FCSTD DOCUMENT  (FreeCAD 1.1R42325 (Git))
Label: flat32
License: All rights reserved
objects: App::FeaturePython×50, Part::Part2DObjectPython×30, Sketcher::SketchObject×2, Image::ImagePlane×2, PartDesign::Body×1, Measure::MeasureDistanceDetached×1, App::Point×1
note: 35 computed .brp shape members not serialized (recipe doc carries the construction recipe); baked Part::Feature solids carry a one-line shape summary decoded from their .brp

FEATURE [Sketcher::SketchObject] Sketch
  ArcFitTolerance = 0
  AttachmentSupport = -> [XY_Plane]
  ExternalTypes = [0]
  FullyConstrained = false
  MakeInternals = false
  MapMode = 5
  sketch-geometry (129):
    g0: LineSegment StartX=-58.4533 StartY=41.9964 StartZ=0 EndX=59.4113 EndY=41.9964 EndZ=0
    g1: LineSegment StartX=72.1645 StartY=11.1126 StartZ=0 EndX=72.1645 EndY=-32.2771 EndZ=0
    g2: LineSegment StartX=-52.8636 StartY=37.943 StartZ=0 EndX=-12.1113 EndY=37.943 EndZ=0
    g3: LineSegment StartX=55.7454 StartY=36.2995 StartZ=0 EndX=55.7454 EndY=9.20361 EndZ=0
    g4: LineSegment StartX=-54.4028 StartY=-1.00339 StartZ=0 EndX=-54.4028 EndY=5.82203 EndZ=0
    g5: LineSegment StartX=-52.8636 StartY=37.943 StartZ=0 EndX=-52.8636 EndY=36.404 EndZ=0
    g6: LineSegment StartX=-52.8636 StartY=36.404 StartZ=0 EndX=-54.3721 EndY=36.404 EndZ=0
    g7: LineSegment StartX=21.2988 StartY=37.9406 StartZ=0 EndX=21.2988 EndY=20.6044 EndZ=0
    g8: LineSegment StartX=21.2988 StartY=20.6044 StartZ=0 EndX=11.216 EndY=20.6044 EndZ=0
    g9: LineSegment StartX=3.2959 StartY=21.0156 StartZ=0 EndX=3.2959 EndY=37.9443 EndZ=0
    g10: LineSegment StartX=20.18 StartY=36.5128 StartZ=0 EndX=20.18 EndY=21.0155 EndZ=0
    g11: LineSegment StartX=20.18 StartY=21.0155 StartZ=0 EndX=4.08358 EndY=21.0155 EndZ=0
    g12: LineSegment StartX=4.08358 StartY=21.0155 StartZ=0 EndX=4.08358 EndY=32.5222 EndZ=0
    g13: LineSegment StartX=11.116 StartY=37.9186 StartZ=0 EndX=11.116 EndY=32.5222 EndZ=0
    g14: LineSegment StartX=11.116 StartY=32.5222 StartZ=0 EndX=4.08358 EndY=32.5222 EndZ=0
    g15: LineSegment StartX=20.18 StartY=36.5128 StartZ=0 EndX=17.2316 EndY=36.5128 EndZ=0
    g16: LineSegment StartX=17.2316 StartY=36.5128 StartZ=0 EndX=17.2316 EndY=37.9186 EndZ=0
    g17: LineSegment StartX=11.116 StartY=37.9186 StartZ=0 EndX=17.2316 EndY=37.9186 EndZ=0
    g18: LineSegment StartX=21.2988 StartY=37.9406 StartZ=0 EndX=54.1032 EndY=37.9406 EndZ=0
    g19: LineSegment StartX=17.7483 StartY=21.0155 StartZ=0 EndX=17.7483 EndY=20.6044 EndZ=0
    g20: LineSegment StartX=11.216 StartY=20.6044 StartZ=0 EndX=11.216 EndY=21.0155 EndZ=0
    g21: LineSegment StartX=-10.9815 StartY=36.5115 StartZ=0 EndX=-10.9815 EndY=21.0156 EndZ=0
    g22: LineSegment StartX=-12.1113 StartY=8.35302 StartZ=0 EndX=-12.1113 EndY=37.943 EndZ=0
    g23: LineSegment StartX=-8.04197 StartY=37.9443 StartZ=0 EndX=-8.04197 EndY=36.5115 EndZ=0
    g24: LineSegment StartX=-8.04197 StartY=36.5115 StartZ=0 EndX=-10.9815 EndY=36.5115 EndZ=0
    g25: LineSegment StartX=-8.04197 StartY=37.9443 StartZ=0 EndX=3.2959 EndY=37.9443 EndZ=0
    g26: LineSegment StartX=-10.9815 StartY=21.0156 StartZ=0 EndX=3.2959 EndY=21.0156 EndZ=0
    g27: LineSegment StartX=11.216 StartY=20.6044 StartZ=0 EndX=-10.9715 EndY=20.6044 EndZ=0
    g28: LineSegment StartX=-10.9715 StartY=20.6044 StartZ=0 EndX=-10.9715 EndY=8.56171 EndZ=0
    g29: LineSegment StartX=-52.8709 StartY=8.97844 StartZ=0 EndX=-54.4014 EndY=8.97844 EndZ=0
    g30: LineSegment StartX=-54.4028 StartY=5.82203 StartZ=0 EndX=-52.8709 EndY=5.82203 EndZ=0
    g31: LineSegment StartX=-52.8709 StartY=5.82203 StartZ=0 EndX=-52.8709 EndY=6.21907 EndZ=0
    g32: LineSegment StartX=-52.8709 StartY=8.35302 StartZ=0 EndX=-12.1113 EndY=8.35302 EndZ=0
    g33: LineSegment StartX=-8.83892 StartY=6.21907 StartZ=0 EndX=-52.8709 EndY=6.21907 EndZ=0
    g34: LineSegment StartX=-10.9715 StartY=8.56171 StartZ=0 EndX=8.9857 EndY=8.56171 EndZ=0
    g35: LineSegment StartX=6.71846 StartY=3.07262 StartZ=0 EndX=-8.83892 EndY=3.07262 EndZ=0
    g36: LineSegment StartX=-8.83892 StartY=3.07262 StartZ=0 EndX=-8.83892 EndY=6.21907 EndZ=0
    g37: LineSegment StartX=-54.4014 StartY=8.97844 StartZ=0 EndX=-54.4028 EndY=36.404 EndZ=0
    g38: LineSegment StartX=-52.8709 StartY=8.35302 StartZ=0 EndX=-52.8709 EndY=8.97844 EndZ=0
    g39: LineSegment StartX=-72.0313 StartY=8.51763 StartZ=0 EndX=-58.4517 EndY=8.51763 EndZ=0
    g40: LineSegment StartX=-58.4517 StartY=6.82057 StartZ=0 EndX=-68.6696 EndY=6.82057 EndZ=0
    g41: LineSegment StartX=-68.6696 StartY=6.82057 StartZ=0 EndX=-68.6696 EndY=5.21862 EndZ=0
    g42: LineSegment StartX=-68.6696 StartY=5.21862 StartZ=0 EndX=-72.0313 EndY=5.21862 EndZ=0
    g43: LineSegment StartX=-72.0313 StartY=5.21862 StartZ=0 EndX=-72.0313 EndY=8.51763 EndZ=0
    g44: LineSegment StartX=-58.4517 StartY=-1.00339 StartZ=0 EndX=-54.4028 EndY=-1.00339 EndZ=0
    g45: LineSegment StartX=-58.4533 StartY=8.51763 StartZ=0 EndX=-58.4533 EndY=41.9964 EndZ=0
    g46: LineSegment StartX=-58.4517 StartY=6.82057 StartZ=0 EndX=-58.4517 EndY=-1.00339 EndZ=0
    g47: LineSegment StartX=8.97848 StartY=-28.496 StartZ=0 EndX=6.71846 EndY=-28.496 EndZ=0
    g48: LineSegment StartX=6.71846 StartY=-28.496 StartZ=0 EndX=6.71846 EndY=3.07262 EndZ=0
    g49: LineSegment StartX=8.9857 StartY=-22.0949 StartZ=0 EndX=9.78167 EndY=-22.0949 EndZ=0
    g50: LineSegment StartX=18.1214 StartY=-23.9331 StartZ=0 EndX=17.1396 EndY=-23.9331 EndZ=0
    g51: LineSegment StartX=8.97848 StartY=-28.496 StartZ=0 EndX=8.97848 EndY=-23.9331 EndZ=0
    g52: LineSegment StartX=8.9857 StartY=-22.0949 StartZ=0 EndX=8.9857 EndY=8.56171 EndZ=0
    g53: LineSegment StartX=17.1396 StartY=-22.0949 StartZ=0 EndX=17.1396 EndY=-23.9331 EndZ=0
    g54: LineSegment StartX=9.78167 StartY=-23.9331 StartZ=0 EndX=9.78167 EndY=-22.0949 EndZ=0
    g55: LineSegment StartX=9.78167 StartY=-23.9331 StartZ=0 EndX=8.97848 EndY=-23.9331 EndZ=0
    g56: LineSegment StartX=17.1396 StartY=-22.0949 StartZ=0 EndX=18.0438 EndY=-22.0949 EndZ=0
    g57: LineSegment StartX=18.0438 StartY=-21.4909 StartZ=0 EndX=21.002 EndY=-21.4909 EndZ=0
    g58: LineSegment StartX=18.0438 StartY=-22.0949 StartZ=0 EndX=18.0438 EndY=-21.4909 EndZ=0
    g59: LineSegment StartX=21.404 StartY=-23.9482 StartZ=0 EndX=21.404 EndY=-24.7569 EndZ=0
    g60: LineSegment StartX=21.404 StartY=-24.7569 StartZ=0 EndX=18.1214 EndY=-24.7569 EndZ=0
    g61: LineSegment StartX=18.1214 StartY=-24.7569 StartZ=0 EndX=18.1214 EndY=-23.9331 EndZ=0
    g62: LineSegment StartX=21.404 StartY=-23.9482 StartZ=0 EndX=25.4966 EndY=-23.9482 EndZ=0
    g63: LineSegment StartX=25.4966 StartY=-23.9482 StartZ=0 EndX=25.4966 EndY=-28.0142 EndZ=0
    g64: LineSegment StartX=27.1081 StartY=-28.0142 StartZ=0 EndX=25.4966 EndY=-28.0142 EndZ=0
    g65: LineSegment StartX=27.1081 StartY=-24.1438 StartZ=0 EndX=27.1081 EndY=-28.0142 EndZ=0
    g66: LineSegment StartX=42.9002 StartY=-24.1438 StartZ=0 EndX=27.1081 EndY=-24.1438 EndZ=0
    g67: LineSegment StartX=42.9002 StartY=-24.9375 StartZ=0 EndX=42.9002 EndY=-24.1438 EndZ=0
    g68: LineSegment StartX=46.1598 StartY=-24.9375 StartZ=0 EndX=42.9002 EndY=-24.9375 EndZ=0
    g69: LineSegment StartX=46.1598 StartY=-24.1343 StartZ=0 EndX=46.1598 EndY=-24.9375 EndZ=0
    g70: LineSegment StartX=67.0505 StartY=-24.1343 StartZ=0 EndX=46.1598 EndY=-24.1343 EndZ=0
    g71: LineSegment StartX=67.0505 StartY=-24.9529 StartZ=0 EndX=67.0505 EndY=-24.1343 EndZ=0
    g72: LineSegment StartX=68.5857 StartY=-24.9529 StartZ=0 EndX=67.0505 EndY=-24.9529 EndZ=0
    g73: LineSegment StartX=68.5857 StartY=-32.2771 StartZ=0 EndX=68.5857 EndY=-24.9529 EndZ=0
    g74: LineSegment StartX=68.5824 StartY=-18.1367 StartZ=0 EndX=72.1645 EndY=-18.1367 EndZ=0
    g75: LineSegment StartX=72.1645 StartY=-32.2771 StartZ=0 EndX=68.5857 EndY=-32.2771 EndZ=0
    g76: LineSegment StartX=68.5824 StartY=5.76906 StartZ=0 EndX=66.9498 EndY=5.76906 EndZ=0
    g77: LineSegment StartX=66.9285 StartY=-21.3814 StartZ=0 EndX=68.5824 EndY=-21.3814 EndZ=0
    g78: LineSegment StartX=68.5824 StartY=-21.3814 StartZ=0 EndX=68.5824 EndY=5.76906 EndZ=0
    g79: LineSegment StartX=66.9285 StartY=-22.3002 StartZ=0 EndX=45.9729 EndY=-22.3002 EndZ=0
    g80: LineSegment StartX=45.9729 StartY=-22.3002 StartZ=0 EndX=45.9729 EndY=-21.6864 EndZ=0
    g81: LineSegment StartX=66.9285 StartY=-21.3814 StartZ=0 EndX=66.9285 EndY=-22.3002 EndZ=0
    g82: LineSegment StartX=38.6082 StartY=-22.2862 StartZ=0 EndX=42.7166 EndY=-22.2862 EndZ=0
    g83: LineSegment StartX=42.7166 StartY=-22.2862 StartZ=0 EndX=42.7166 EndY=-21.6864 EndZ=0
    g84: LineSegment StartX=38.6082 StartY=-4.46395 StartZ=0 EndX=38.6082 EndY=-22.2862 EndZ=0
    g85: LineSegment StartX=45.9729 StartY=-21.6864 StartZ=0 EndX=42.7166 EndY=-21.6864 EndZ=0
    g86: LineSegment StartX=-58.4533 StartY=33.1051 StartZ=0 EndX=-54.4027 EndY=33.1051 EndZ=0
    g87: LineSegment StartX=-54.4018 StartY=16.0181 StartZ=0 EndX=-58.4533 EndY=16.0181 EndZ=0
    g88: LineSegment StartX=-22.6875 StartY=41.9964 StartZ=0 EndX=-22.6875 EndY=37.943 EndZ=0
    g89: LineSegment StartX=-39.8263 StartY=37.943 StartZ=0 EndX=-39.8263 EndY=41.9964 EndZ=0
    g90: LineSegment StartX=-0.273217 StartY=21.0156 StartZ=0 EndX=-0.273217 EndY=20.6044 EndZ=0
    g91: LineSegment StartX=-6.8366 StartY=20.6044 StartZ=0 EndX=-6.8366 EndY=21.0156 EndZ=0
    g92: LineSegment StartX=21.002 StartY=-4.46395 StartZ=0 EndX=38.6082 EndY=-4.46395 EndZ=0
    g93: LineSegment StartX=39.5091 StartY=-22.2862 StartZ=0 EndX=39.5091 EndY=-22.8134 EndZ=0
    g94: LineSegment StartX=21.002 StartY=-21.4909 StartZ=0 EndX=21.002 EndY=-4.46395 EndZ=0
    g95: LineSegment StartX=21.6887 StartY=-5.08078 StartZ=0 EndX=37.4984 EndY=-5.08078 EndZ=0
    g96: LineSegment StartX=37.4984 StartY=-5.08078 StartZ=0 EndX=37.4984 EndY=-19.1535 EndZ=0
    g97: LineSegment StartX=30.5655 StartY=-21.7835 StartZ=0 EndX=21.6887 EndY=-21.7835 EndZ=0
    g98: LineSegment StartX=21.6887 StartY=-21.7835 StartZ=0 EndX=21.6887 EndY=-5.08078 EndZ=0
    g99: LineSegment StartX=30.5655 StartY=-19.1535 StartZ=0 EndX=37.4984 EndY=-19.1535 EndZ=0
    g100: LineSegment StartX=30.5655 StartY=-21.7835 StartZ=0 EndX=30.5655 EndY=-19.1535 EndZ=0
    g101: LineSegment StartX=72.1645 StartY=-3.43392 StartZ=0 EndX=68.5824 EndY=-3.43392 EndZ=0
    g102: LineSegment StartX=58.5414 StartY=7.46309 StartZ=0 EndX=66.9498 EndY=7.46309 EndZ=0
    g103: LineSegment StartX=66.9498 StartY=7.46309 StartZ=0 EndX=66.9498 EndY=5.76906 EndZ=0
    g104: LineSegment StartX=58.5414 StartY=5.92032 StartZ=0 EndX=58.5414 EndY=7.46309 EndZ=0
    g105: LineSegment StartX=55.2287 StartY=5.92032 StartZ=0 EndX=58.5414 EndY=5.92032 EndZ=0
    g106: LineSegment StartX=55.2287 StartY=7.0292 StartZ=0 EndX=55.2287 EndY=5.92032 EndZ=0
    g107: LineSegment StartX=54.2209 StartY=9.20361 StartZ=0 EndX=55.7454 EndY=9.20361 EndZ=0
    g108: LineSegment StartX=54.2209 StartY=7.0292 StartZ=0 EndX=54.2209 EndY=9.20361 EndZ=0
    g109: LineSegment StartX=55.2287 StartY=7.0292 StartZ=0 EndX=54.2209 EndY=7.0292 EndZ=0
    g110: LineSegment StartX=55.7454 StartY=36.2995 StartZ=0 EndX=54.1032 EndY=36.2995 EndZ=0
    g111: LineSegment StartX=54.1032 StartY=36.2995 StartZ=0 EndX=54.1032 EndY=37.9406 EndZ=0
    g112: LineSegment StartX=55.7454 StartY=28.7724 StartZ=0 EndX=59.4076 EndY=28.7724 EndZ=0
    g113: LineSegment StartX=68.3386 StartY=11.1606 StartZ=0 EndX=55.7454 EndY=11.1606 EndZ=0
    g114: LineSegment StartX=65.906 StartY=38.0345 StartZ=0 EndX=59.4076 EndY=38.0345 EndZ=0
    g115: LineSegment StartX=59.4076 StartY=38.0345 StartZ=0 EndX=59.4076 EndY=11.1606 EndZ=0
    g116: LineSegment StartX=68.3386 StartY=11.1606 StartZ=0 EndX=68.3386 EndY=35.5504 EndZ=0
    g117: LineSegment StartX=65.906 StartY=35.5504 StartZ=0 EndX=68.3386 EndY=35.5504 EndZ=0
    g118: LineSegment StartX=65.906 StartY=38.0345 StartZ=0 EndX=65.906 EndY=35.5504 EndZ=0
    g119: LineSegment StartX=59.4113 StartY=39.6605 StartZ=0 EndX=70.0341 EndY=39.6605 EndZ=0
    g120: LineSegment StartX=59.4113 StartY=41.9964 StartZ=0 EndX=59.4113 EndY=39.6605 EndZ=0
    g121: LineSegment StartX=70.0341 StartY=11.1126 StartZ=0 EndX=72.3705 EndY=11.1126 EndZ=0
    g122: LineSegment StartX=70.0341 StartY=39.6605 StartZ=0 EndX=70.0341 EndY=11.1126 EndZ=0
    g123: LineSegment StartX=40.6854 StartY=41.9964 StartZ=0 EndX=40.6854 EndY=37.9406 EndZ=0
    g124: LineSegment StartX=23.5435 StartY=37.9406 StartZ=0 EndX=23.5435 EndY=41.9964 EndZ=0
    g125: LineSegment StartX=-12.1113 StartY=17.5417 StartZ=0 EndX=-10.9715 EndY=17.5417 EndZ=0
    g126: LineSegment StartX=-10.9715 StartY=10.2112 StartZ=0 EndX=-12.1113 EndY=10.2112 EndZ=0
    g127: LineSegment StartX=21.002 StartY=-19.139 StartZ=0 EndX=21.6887 EndY=-19.139 EndZ=0
    g128: LineSegment StartX=21.6887 StartY=-11.4103 StartZ=0 EndX=21.002 EndY=-11.4103 EndZ=0
  constraints (270):
    c: Coincident(g45,g0)
    c: Horizontal(g0)
    c: Vertical(g1)
    c: Horizontal(g2)
    c: Vertical(g3)
    c: Vertical(g4)
    c: Coincident(g5,g6)
    c: PointOnObject(g37,g6)
    c: Coincident(g5,g2)
    c: Perpendicular(g5,g6)
    c: Perpendicular(g6,g4)
    c: Coincident(g7,g8)
    c: Horizontal(g8)
    c: Vertical(g7)
    c: Vertical(g9)
    c: Coincident(g10,g11)
    c: Coincident(g11,g12)
    c: Horizontal(g11)
    c: Vertical(g10)
    c: Vertical(g12)
    c: Coincident(g13,g14)
    c: Horizontal(g14)
    c: Vertical(g13)
    c: Coincident(g15,g16)
    c: Horizontal(g15)
    c: Vertical(g16)
    c: Coincident(g17,g13)
    c: Coincident(g25,g9)
    c: Coincident(g14,g12)
    c: Coincident(g17,g16)
    c: Coincident(g15,g10)
    c: Coincident(g7,g18)
    c: Perpendicular(g18,g7)
    c: Vertical(g19)
    c: Vertical(g20)
    c: PointOnObject(g20,g11)
    c: PointOnObject(g19,g11)
    c: PointOnObject(g19,g8)
    c: Vertical(g21)
    c: Vertical(g22)
    c: Coincident(g23,g24)
    c: Horizontal(g24)
    c: Vertical(g23)
    c: Coincident(g2,g22)
    c: Coincident(g21,g24)
    c: Coincident(g23,g25)
    c: Horizontal(g26)
    c: Horizontal(g27)
    c: Coincident(g9,g26)
    c: Coincident(g21,g26)
    c: Coincident(g28,g27)
    c: Coincident(g8,g20)
    c: Coincident(g27,g8)
    c: Coincident(g30,g31)
    c: Coincident(g38,g29)
    c: Horizontal(g29)
    c: Horizontal(g30)
    c: Vertical(g31)
    c: Horizontal(g32)
    c: Horizontal(g33)
    c: Horizontal(g34)
    c: Coincident(g35,g36)
    c: Horizontal(g35)
    c: Vertical(g36)
    c: Coincident(g33,g36)
    c: Coincident(g30,g4)
    c: Coincident(g29,g37)
    c: Coincident(g31,g33)
    c: Coincident(g38,g32)
    c: Horizontal(g39)
    c: Horizontal(g40)
    c: Coincident(g41,g42)
    c: Coincident(g42,g43)
    c: Horizontal(g42)
    c: Vertical(g41)
    c: Vertical(g43)
    c: Horizontal(g44)
    c: Coincident(g41,g40)
    c: Coincident(g39,g43)
    c: PointOnObject(g45,g39)
    c: Coincident(g46,g40)
    c: Vertical(g46)
    c: Coincident(g4,g44)
    c: Coincident(g47,g48)
    c: Horizontal(g47)
    c: Vertical(g48)
    c: Coincident(g48,g35)
    c: Horizontal(g49)
    c: Horizontal(g50)
    c: Vertical(g51)
    c: Coincident(g51,g47)
    c: Coincident(g51,g55)
    c: Coincident(g52,g49)
    c: Coincident(g34,g52)
    c: Vertical(g52)
    c: Vertical(g53)
    c: Vertical(g54)
    c: Coincident(g50,g53)
    c: Coincident(g55,g54)
    c: Coincident(g49,g54)
    c: Coincident(g56,g53)
    c: Coincident(g58,g57)
    c: Horizontal(g57)
    c: Vertical(g58)
    c: Coincident(g59,g60)
    c: Coincident(g60,g61)
    c: Horizontal(g60)
    c: Vertical(g59)
    c: Vertical(g61)
    c: Coincident(g62,g63)
    c: Horizontal(g62)
    c: Vertical(g63)
    c: Coincident(g65,g64)
    c: Horizontal(g64)
    c: Vertical(g65)
    c: Coincident(g67,g66)
    c: Horizontal(g66)
    c: Vertical(g67)
    c: Coincident(g69,g68)
    c: Horizontal(g68)
    c: Vertical(g69)
    c: Coincident(g71,g70)
    c: Horizontal(g70)
    c: Vertical(g71)
    c: Coincident(g56,g58)
    c: Coincident(g61,g50)
    c: Coincident(g59,g62)
    c: Coincident(g66,g65)
    c: Coincident(g63,g64)
    c: Coincident(g68,g67)
    c: Coincident(g69,g70)
    c: Coincident(g73,g72)
    c: Horizontal(g72)
    c: Vertical(g73)
    c: Horizontal(g74)
    c: Horizontal(g75)
    c: Coincident(g77,g78)
    c: Coincident(g78,g76)
    c: Horizontal(g76)
    c: Horizontal(g77)
    c: Vertical(g78)
    c: Coincident(g79,g80)
    c: Coincident(g81,g79)
    c: Horizontal(g79)
    c: Vertical(g80)
    c: Vertical(g81)
    c: Coincident(g82,g83)
    c: Coincident(g84,g82)
    c: Horizontal(g82)
    c: Vertical(g83)
    c: Vertical(g84)
    c: Horizontal(g85)
    c: Coincident(g83,g85)
    c: Coincident(g85,g80)
    c: Coincident(g81,g77)
    c: PointOnObject(g74,g78)
    c: PointOnObject(g74,g1)
    c: Coincident(g73,g75)
    c: Coincident(g72,g71)
    c: Coincident(g75,g1)
    c: Horizontal(g86)
    c: Horizontal(g87)
    c: PointOnObject(g87,g45)
    c: PointOnObject(g87,g37)
    c: PointOnObject(g86,g45)
    c: PointOnObject(g86,g37)
    c: Vertical(g88)
    c: Vertical(g89)
    c: PointOnObject(g88,g0)
    c: PointOnObject(g88,g2)
    c: PointOnObject(g89,g2)
    c: PointOnObject(g89,g0)
    c: Vertical(g90)
    c: Vertical(g91)
    c: PointOnObject(g90,g26)
    c: PointOnObject(g90,g27)
    c: PointOnObject(g91,g26)
    c: PointOnObject(g91,g27)
    c: Coincident(g94,g92)
    c: Horizontal(g92)
    c: Vertical(g93)
    c: Vertical(g94)
    c: Coincident(g95,g96)
    c: Coincident(g97,g98)
    c: Coincident(g98,g95)
    c: Horizontal(g95)
    c: Horizontal(g97)
    c: Vertical(g96)
    c: Vertical(g98)
    c: Coincident(g100,g99)
    c: Horizontal(g99)
    c: Vertical(g100)
    c: Coincident(g97,g100)
    c: Coincident(g99,g96)
    c: Coincident(g94,g57)
    c: PointOnObject(g93,g82)
    c: Coincident(g84,g92)
    c: Horizontal(g101)
    c: PointOnObject(g101,g78)
    c: PointOnObject(g101,g1)
    c: Coincident(g102,g103)
    c: Coincident(g104,g102)
    c: Horizontal(g102)
    c: Vertical(g103)
    c: Vertical(g104)
    c: Coincident(g106,g105)
    c: Horizontal(g105)
    c: Vertical(g106)
    c: Coincident(g109,g108)
    c: Coincident(g108,g107)
    c: Horizontal(g107)
    c: Vertical(g108)
    c: Coincident(g107,g3)
    c: Coincident(g109,g106)
    c: Coincident(g104,g105)
    c: Coincident(g103,g76)
    c: Coincident(g110,g111)
    c: Horizontal(g110)
    c: Vertical(g111)
    c: Coincident(g18,g111)
    c: Coincident(g110,g3)
    c: Horizontal(g112)
    c: Horizontal(g113)
    c: Coincident(g114,g115)
    c: Horizontal(g114)
    c: Vertical(g115)
    c: Vertical(g116)
    c: Coincident(g118,g117)
    c: Horizontal(g117)
    c: Vertical(g118)
    c: Coincident(g117,g116)
    c: Coincident(g118,g114)
    c: PointOnObject(g112,g115)
    c: PointOnObject(g112,g3)
    c: PointOnObject(g113,g3)
    c: PointOnObject(g115,g113)
    c: Coincident(g113,g116)
    c: Coincident(g120,g119)
    c: Horizontal(g119)
    c: Vertical(g120)
    c: Coincident(g122,g121)
    c: Horizontal(g121)
    c: Vertical(g122)
    c: Coincident(g0,g120)
    c: Coincident(g119,g122)
    c: PointOnObject(g1,g121)
    c: Vertical(g123)
    c: Vertical(g124)
    c: PointOnObject(g123,g0)
    c: PointOnObject(g123,g18)
    c: PointOnObject(g124,g0)
    c: PointOnObject(g124,g18)
    c: Vertical(g28)
    c: Coincident(g22,g32)
    c: Coincident(g28,g34)
    c: Horizontal(g125)
    c: Horizontal(g126)
    c: PointOnObject(g126,g22)
    c: PointOnObject(g126,g28)
    c: PointOnObject(g125,g22)
    c: PointOnObject(g125,g28)
    c: Horizontal(g127)
    c: Horizontal(g128)
    c: PointOnObject(g128,g94)
    c: PointOnObject(g128,g98)
    c: PointOnObject(g127,g94)
    c: PointOnObject(g127,g98)
    c: DistanceY(g22,g22) = 29.59
    c: Distance(g22,g37) = 42.29
    c: Horizontal(g17)
FEATURE [PartDesign::Body] Body
  AllowCompound = false
  Group = -> [Sketch]
  Origin = -> Origin
FEATURE [Part::Part2DObjectPython] Clone2D  label="Sketch (2D)"  # Draft 2D object (typed FeaturePython)
  Fuse = false
  Objects = -> [Sketch]
  Scale = (122,122,122)
FEATURE [Image::ImagePlane] flat033
  XSize = 149.073
  YSize = 109.677
FEATURE [App::FeaturePython] Dimension  # Draft dimension (typed FeaturePython)
  Diameter = false
  Dimline = (-2854.54,1806.14,0)
  Direction = (0,0,0)
  Distance = 3622.43
  End = (-1477.69,1008.44,0)
  Normal = (0,0,1)
  Start = (-1477.69,4630.87,0)
FEATURE [App::FeaturePython] Dimension001  # Draft dimension (typed FeaturePython)
  Diameter = false
  Dimline = (6194.79,-201.526,0)
  Direction = (0,0,0)
  Distance = 2371.58
  End = (6625.96,853.939,0)
  Normal = (0,0,1)
  Start = (4712.65,-547.359,0)
FEATURE [Part::Part2DObjectPython] Rectangle  # Draft 2D object (typed FeaturePython)
  Area = 1.27559e+06
  ChamferSize = 0
  Columns = 1
  FilletRadius = 0
  Height = 1456.71
  Length = 875.663
  MakeFace = true
  Placement = pos=(7956.71,-832.865,0) rot=(0,0,1;1.5708rad)
  Rows = 1
FEATURE [Part::Part2DObjectPython] Rectangle001  # Draft 2D object (typed FeaturePython)
  Area = 1.27485e+06
  ChamferSize = 0
  Columns = 1
  FilletRadius = 0
  Height = 1923.18
  Length = 662.884
  MakeFace = true
  Placement = pos=(4784.29,-2496.31,0) rot=(0,0,1;0rad)
  Rows = 1
FEATURE [Part::Part2DObjectPython] Rectangle002  # Draft 2D object (typed FeaturePython)
  Area = 1.72525e+06
  ChamferSize = 0
  Columns = 1
  FilletRadius = 0
  Height = 654.7
  Length = 2635.17
  MakeFace = true
  Placement = pos=(5496.27,-2561.78,0) rot=(0,0,1;0rad)
  Rows = 1
FEATURE [Part::Part2DObjectPython] Rectangle006  # Draft 2D object (typed FeaturePython)
  Area = 833413
  ChamferSize = 0
  Columns = 1
  FilletRadius = 0
  Height = 455.621
  Length = 1829.18
  MakeFace = true
  Placement = pos=(2767.78,-510.925,0) rot=(0,0,1;0rad)
  Rows = 1
FEATURE [Part::Part2DObjectPython] Rectangle010  # Draft 2D object (typed FeaturePython)
  Area = 1.30156e+06
  ChamferSize = 0
  Columns = 1
  FilletRadius = 0
  Height = 2000.12
  Length = 650.74
  MakeFace = true
  Placement = pos=(-2129.21,2192.92,0) rot=(0,0,1;0rad)
  Rows = 1
FEATURE [Part::Part2DObjectPython] Rectangle011  # Draft 2D object (typed FeaturePython)
  Area = 2632188
  ChamferSize = 0
  Columns = 1
  FilletRadius = 0
  Height = 1880
  Length = 1400.1
  MakeFace = true
  Placement = pos=(-4543.16,1040.33,0) rot=(0,0,1;0rad)
  Rows = 1
FEATURE [Part::Part2DObjectPython] Rectangle012  # Draft 2D object (typed FeaturePython)
  Area = 732013
  ChamferSize = 0
  Columns = 1
  FilletRadius = 0
  Height = 609.737
  Length = 1200.54
  MakeFace = true
  Placement = pos=(-6502.33,1684,0) rot=(0,0,1;0rad)
  Rows = 1
FEATURE [Part::Part2DObjectPython] Rectangle013  # Draft 2D object (typed FeaturePython)
  Area = 850265
  ChamferSize = 0
  Columns = 1
  FilletRadius = 0
  Height = 459.801
  Length = 1849.2
  MakeFace = true
  Placement = pos=(-4771.15,4096.59,0) rot=(0,0,1;0rad)
  Rows = 1
FEATURE [App::FeaturePython] Dimension002  # Draft dimension (typed FeaturePython)
  Diameter = false
  Dimline = (4845.95,4276.18,0)
  Direction = (0,0,0)
  Distance = 2085.32
  End = (4959.33,4626.19,0)
  Normal = (0,0,1)
  Start = (2874.01,4626.19,0)
FEATURE [App::FeaturePython] Dimension003  # Draft dimension (typed FeaturePython)
  Diameter = false
  Dimline = (-3021.5,4294.46,0)
  Direction = (0,0,0)
  Distance = 2088.74
  End = (-2767.22,4627.45,0)
  Normal = (0,0,1)
  Start = (-4855.96,4627.45,0)
FEATURE [App::FeaturePython] Dimension004  # Draft dimension (typed FeaturePython)
  Diameter = false
  Dimline = (-6208.59,1996.06,0)
  Direction = (0,0,0)
  Distance = 2083.38
  End = (-6636.1,1953.91,0)
  Normal = (0,0,1)
  Start = (-6636.1,4037.28,0)
FEATURE [App::FeaturePython] Dimension005  # Draft dimension (typed FeaturePython)
  Diameter = false
  Dimline = (7840.76,-2175.53,0)
  Direction = (0,0,0)
  Distance = 1785.32
  End = (8367.62,-2208.65,0)
  Normal = (0,0,1)
  Start = (8367.62,-423.327,0)
FEATURE [App::FeaturePython] Dimension006  # Draft dimension (typed FeaturePython)
  Diameter = false
  Dimline = (6407.54,1358.86,0)
  Direction = (0,0,0)
  Distance = 2158.53
  End = (6801,1351.5,0)
  Normal = (0,0,1)
  Start = (6801,3510.03,0)
FEATURE [App::FeaturePython] Dimension007  # Draft dimension (typed FeaturePython)
  Diameter = false
  Dimline = (2086.67,4371.72,0)
  Direction = (0,0,0)
  Distance = 744.477
  End = (2099.36,4625.62,0)
  Normal = (0,0,1)
  Start = (1354.88,4625.62,0)
FEATURE [Part::Part2DObjectPython] Rectangle015  # Draft 2D object (typed FeaturePython)
  Area = 707177
  ChamferSize = 0
  Columns = 1
  FilletRadius = 0
  Height = 589.235
  Length = 1200.16
  MakeFace = true
  Placement = pos=(-6447.74,3373.47,0) rot=(0,0,1;0rad)
  Rows = 1
FEATURE [App::FeaturePython] Dimension008  # Draft dimension (typed FeaturePython)
  Diameter = false
  Dimline = (-2339.12,2134.76,0)
  Direction = (0,0,0)
  Distance = 2489.46
  End = (-1486.01,2134.76,0)
  Normal = (0,0,1)
  Start = (-1482.33,4624.22,0)
FEATURE [App::FeaturePython] Dimension009  # Draft dimension (typed FeaturePython)
  Diameter = false
  Dimline = (6598.51,3522.63,0)
  Direction = (0,0,0)
  Distance = 900
  End = (6800,3500,0)
  Normal = (0,0,1)
  Start = (6800,4400,0)
FEATURE [App::FeaturePython] Dimension010  # Draft dimension (typed FeaturePython)
  Diameter = false
  Dimline = (8282.17,3828.92,0)
  Direction = (0,0,0)
  Distance = 1092.13
  End = (8341.01,4200.32,0)
  Normal = (0,0,1)
  Start = (7248.88,4200.32,0)
FEATURE [App::FeaturePython] Dimension011  # Draft dimension (typed FeaturePython)
  Diameter = false
  Dimline = (8000,4200,0)
  Direction = (0,0,0)
  Distance = 794.276
  End = (8043.15,4395.21,0)
  Normal = (0,0,1)
  Start = (7248.88,4395.21,0)
FEATURE [App::FeaturePython] Dimension012  # Draft dimension (typed FeaturePython)
  Diameter = false
  Dimline = (7787.35,1363.16,0)
  Direction = (0,0,0)
  Distance = 3269.7
  End = (7248.39,1363.16,0)
  Normal = (0,0,1)
  Start = (7248.39,4632.86,0)
FEATURE [Part::Part2DObjectPython] Wire  # Draft 2D object (typed FeaturePython)
  Area = 0
  ChamferSize = 0
  Closed = false
  End = (-6400,3700,0)
  FilletRadius = 0
  Length = 6200
  MakeFace = true
  Placement = pos=(-1500,2400,0) rot=(0,0,1;0rad)
  Points = (4) [(0,0,0),(-900,0,0),(-900,1300,0),(-4900,1300,0)]
  Start = (-1500,2400,0)
  Subdivisions = 0
FEATURE [App::FeaturePython] Dimension013  # Draft dimension (typed FeaturePython)
  Diameter = false
  Dimline = (-5400,4500,0)
  Direction = (0,0,0)
  Distance = 600
  End = (-5700,4000,0)
  Normal = (0,0,1)
  Start = (-5700,4600,0)
FEATURE [App::FeaturePython] Dimension014  # Draft dimension (typed FeaturePython)
  Diameter = false
  Dimline = (8200,-1600,0)
  Direction = (0,0,0)
  Distance = 1700
  End = (8300,-2500,0)
  Normal = (0,0,1)
  Start = (8300,-800,0)
FEATURE [Sketcher::SketchObject] Sketch001
  ArcFitTolerance = 0
  ExternalTypes = [0]
  FullyConstrained = true
  MakeInternals = false
FEATURE [Measure::MeasureDistanceDetached] Distance  label="Distance: 6568.63 mm"
  Distance = 6568.63
  DistanceX = 6567.14
  DistanceY = 139.939
  DistanceZ = 0
  Position1 = (1093.73,-2248.34,0)
  Position2 = (7660.87,-2388.28,0)
FEATURE [Part::Part2DObjectPython] Line  # Draft 2D object (typed FeaturePython)
  Area = 0
  ChamferSize = 0
  Closed = false
  End = (-6249.14,4623.07,0)
  FilletRadius = 0
  Length = 529.719
  MakeFace = true
  Placement = pos=(-6639.07,4264.53,0) rot=(0,0,1;0rad)
  Points = (2) [(0,0,0),(389.936,358.542,0)]
  Start = (-6639.07,4264.53,0)
  Subdivisions = 0
FEATURE [Part::Part2DObjectPython] Line001  # Draft 2D object (typed FeaturePython)
  Area = 0
  ChamferSize = 0
  Closed = false
  End = (6797.11,4214.68,0)
  FilletRadius = 0
  Length = 578.325
  MakeFace = true
  Placement = pos=(6388.17,4623.62,0) rot=(0,0,1;0rad)
  Points = (2) [(0,0,0),(408.938,-408.938,0)]
  Start = (6388.17,4623.62,0)
  Subdivisions = 0
FEATURE [Part::Part2DObjectPython] Line002  # Draft 2D object (typed FeaturePython)
  Area = 0
  ChamferSize = 0
  Closed = false
  End = (4400,4600,0)
  FilletRadius = 0
  Length = 1200
  MakeFace = true
  Placement = pos=(3200,4600,0) rot=(0,0,1;0rad)
  Points = (2) [(0,0,0),(1200,0,0)]
  Start = (3200,4600,0)
  Subdivisions = 0
FEATURE [Part::Part2DObjectPython] Line003  # Draft 2D object (typed FeaturePython)
  Area = 0
  ChamferSize = 0
  Closed = false
  End = (5100,4600,0)
  FilletRadius = 0
  Length = 1200
  MakeFace = true
  Placement = pos=(6300,4600,0) rot=(0,0,1;0rad)
  Points = (2) [(0,0,0),(-1200,0,0)]
  Start = (6300,4600,0)
  Subdivisions = 0
FEATURE [Part::Part2DObjectPython] Line004  # Draft 2D object (typed FeaturePython)
  Area = 0
  ChamferSize = 0
  Closed = false
  End = (4500,4600,0)
  FilletRadius = 0
  Length = 500
  MakeFace = true
  Placement = pos=(5000,4600,0) rot=(0,0,1;0rad)
  Points = (2) [(0,0,0),(-500,0,0)]
  Start = (5000,4600,0)
  Subdivisions = 0
FEATURE [App::FeaturePython] Dimension015  # Draft dimension (typed FeaturePython)
  Diameter = false
  Dimline = (2300,-200,0)
  Direction = (0,0,0)
  Distance = 5200
  End = (3200,-600,0)
  Normal = (0,0,1)
  Start = (3200,4600,0)
FEATURE [App::FeaturePython] Dimension016  # Draft dimension (typed FeaturePython)
  Diameter = false
  Dimline = (6500,3100,0)
  Direction = (0,0,0)
  Distance = 4200
  End = (6800,4400,0)
  Normal = (0,0,1)
  Start = (2600,4400,0)
FEATURE [App::FeaturePython] Dimension017  # Draft dimension (typed FeaturePython)
  Diameter = false
  Dimline = (6400,4300,0)
  Direction = (0,0,0)
  Distance = 3200
  End = (6400,4500,0)
  Normal = (0,0,1)
  Start = (3200,4500,0)
FEATURE [App::FeaturePython] Dimension018  # Draft dimension (typed FeaturePython)
  Diameter = false
  Dimline = (6400,500,0)
  Direction = (0,0,0)
  Distance = 4152.84
  End = (6600,1000,0)
  Normal = (0,0,1)
  Start = (2447.29,966.029,0)
FEATURE [Part::Part2DObjectPython] Rectangle017  # Draft 2D object (typed FeaturePython)
  Area = 45600
  ChamferSize = 0
  Columns = 1
  FilletRadius = 0
  Height = 760
  Length = 60
  MakeFace = true
  Placement = pos=(2300,800,0) rot=(0,0,1;0rad)
  Rows = 1
FEATURE [App::FeaturePython] Dimension019  # Draft dimension (typed FeaturePython)
  Diameter = false
  Dimline = (2883.44,-2921.19,0)
  Direction = (0,0,0)
  Distance = 259.05
  End = (2797.73,-2921.19,0)
  Normal = (0,0,1)
  Start = (2797.73,-2662.14,0)
FEATURE [App::FeaturePython] Dimension020  # Draft dimension (typed FeaturePython)
  Diameter = false
  Dimline = (2650.24,-2757.17,0)
  Direction = (0,0,0)
  Distance = 87.6201
  End = (2650.24,-2500.02,0)
  Normal = (0,0,1)
  Start = (2562.62,-2500.02,0)
FEATURE [App::FeaturePython] Dimension021  # Draft dimension (typed FeaturePython)
  Diameter = false
  Dimline = (1993.21,-2976.53,0)
  Direction = (0,0,0)
  Distance = 392.14
  End = (2268.84,-3016.31,0)
  Normal = (0,0,1)
  Start = (2268.84,-2624.17,0)
FEATURE [App::FeaturePython] Dimension022  # Draft dimension (typed FeaturePython)
  Diameter = false
  Dimline = (2537.2,-2369.73,0)
  Direction = (0,0,0)
  Distance = 358.099
  End = (2561.96,-2621.16,0)
  Normal = (0,0,1)
  Start = (2203.86,-2621.16,0)
FEATURE [App::FeaturePython] Dimension023  # Draft dimension (typed FeaturePython)
  Diameter = false
  Dimline = (6472.81,855.264,0)
  Direction = (0,0,0)
  Distance = 267.247
  End = (6618.58,855.264,0)
  Normal = (0,0,1)
  Start = (6618.58,1122.51,0)
FEATURE [App::FeaturePython] Dimension024  # Draft dimension (typed FeaturePython)
  Diameter = false
  Dimline = (7104.48,629.666,0)
  Direction = (0,0,0)
  Distance = 406.076
  End = (7135.72,719.905,0)
  Normal = (0,0,1)
  Start = (6729.64,719.905,0)
FEATURE [Part::Part2DObjectPython] Wire002  # Draft 2D object (typed FeaturePython)
  Area = 0
  ChamferSize = 0
  Closed = false
  End = (5100,-2200,0)
  FilletRadius = 0
  Length = 2900
  MakeFace = true
  Placement = pos=(4500,-700,0) rot=(0,0,1;0rad)
  Points = (6) [(0,0,0),(0,-1400,0),(300,-1400,0),(300,-1900,0),(600,-1900,0),(600,-1500,0)]
  Start = (4500,-700,0)
  Subdivisions = 0
FEATURE [App::FeaturePython] Dimension025  # Draft dimension (typed FeaturePython)
  Diameter = false
  Dimline = (1200,-3455.03,0)
  Direction = (0,0,0)
  Distance = 1500
  End = (1200,-3100,0)
  Normal = (0,0,1)
  Start = (2700,-3100,0)
FEATURE [App::FeaturePython] Dimension026  # Draft dimension (typed FeaturePython)
  Diameter = false
  Dimline = (1600,-5400,0)
  Direction = (0,0,0)
  Distance = 2400
  End = (1200,-5400,0)
  Normal = (0,0,1)
  Start = (1200,-3000,0)
FEATURE [App::FeaturePython] Dimension027  # Draft dimension (typed FeaturePython)
  Diameter = false
  Dimline = (3100,-1400,0)
  Direction = (0,0,0)
  Distance = 800
  End = (2700,-1400,0)
  Normal = (0,0,1)
  Start = (2700,-600,0)
FEATURE [Part::Part2DObjectPython] Wire003  # Draft 2D object (typed FeaturePython)
  Area = 0
  ChamferSize = 0
  Closed = false
  End = (1300,-5500,0)
  FilletRadius = 0
  Length = 6500
  MakeFace = true
  Placement = pos=(2700,-600,0) rot=(0,0,1;0rad)
  Points = (5) [(0,0,0),(0,-2500,0),(-1400,-2500,0),(-1400,-5000,0),(-1400,-4900,0)]
  Start = (2700,-600,0)
  Subdivisions = 0
FEATURE [App::FeaturePython] Dimension028  # Draft dimension (typed FeaturePython)
  Diameter = false
  Dimline = (-5400,1100,0)
  Direction = (0,0,0)
  Distance = 3600
  End = (-6400,1000,0)
  Normal = (0,0,1)
  Start = (-6400,4600,0)
FEATURE [App::FeaturePython] Dimension029  # Draft dimension (typed FeaturePython)
  Diameter = false
  Dimline = (-2600,2200,0)
  Direction = (0,0,0)
  Distance = 2000
  End = (-1500,2400,0)
  Normal = (0,0,1)
  Start = (-1500,4400,0)
FEATURE [Part::Part2DObjectPython] Line005  # Draft 2D object (typed FeaturePython)
  Area = 0
  ChamferSize = 0
  Closed = false
  End = (-1900,4600,0)
  FilletRadius = 0
  Length = 700
  MakeFace = true
  Placement = pos=(-2600,4600,0) rot=(0,0,1;0rad)
  Points = (2) [(0,0,0),(700,0,0)]
  Start = (-2600,4600,0)
  Subdivisions = 0
FEATURE [Part::Part2DObjectPython] Rectangle018  # Draft 2D object (typed FeaturePython)
  Area = 65946.4
  ChamferSize = 0
  Columns = 1
  FilletRadius = 0
  Height = 236.864
  Length = 278.415
  MakeFace = true
  Placement = pos=(4300,-2336.86,0) rot=(0,0,1;0rad)
  Rows = 1
FEATURE [Part::Part2DObjectPython] Rectangle019  # Draft 2D object (typed FeaturePython)
  Area = 142212
  ChamferSize = 0
  Columns = 1
  FilletRadius = 0
  Height = 312.544
  Length = 455.014
  MakeFace = true
  Placement = pos=(4100,-2012.54,0) rot=(0,0,1;0rad)
  Rows = 1
FEATURE [Part::Part2DObjectPython] Rectangle020  # Draft 2D object (typed FeaturePython)
  Area = 1.1128e+06
  ChamferSize = 0
  Columns = 1
  FilletRadius = 0
  Height = 580.765
  Length = 1916.1
  MakeFace = true
  Placement = pos=(2643.15,-1207.1,0) rot=(0,0,1;0rad)
  Rows = 1
FEATURE [App::FeaturePython] Dimension030  # Draft dimension (typed FeaturePython)
  Diameter = false
  Dimline = (-1400,3700,0)
  Direction = (0,0,0)
  Distance = 5200
  End = (-1400,4200,0)
  Normal = (0,0,1)
  Start = (-6600,4200,0)
FEATURE [App::FeaturePython] Dimension031  # Draft dimension (typed FeaturePython)
  Diameter = false
  Dimline = (5400,3500,0)
  Direction = (0,0,0)
  Distance = 1100
  End = (6500,3500,0)
  Normal = (0,0,1)
  Start = (6500,4600,0)
FEATURE [App::FeaturePython] Dimension032  # Draft dimension (typed FeaturePython)
  Diameter = false
  Dimline = (-5028.36,1049.05,0)
  Direction = (0,0,0)
  Distance = 700
  End = (-5900,1000,0)
  Normal = (0,0,1)
  Start = (-5900,1700,0)
FEATURE [Part::Part2DObjectPython] Rectangle022  # Draft 2D object (typed FeaturePython)
  Area = 100000
  ChamferSize = 0
  Columns = 1
  FilletRadius = 0
  Height = 1000
  Length = 100
  MakeFace = true
  Placement = pos=(2700,2500,0) rot=(0,0,1;0rad)
  Rows = 1
FEATURE [App::FeaturePython] Dimension033  # Draft dimension (typed FeaturePython)
  Diameter = false
  Dimline = (-6019.87,4056.76,0)
  Direction = (0,0,0)
  Distance = 543.242
  End = (-6300,4056.76,0)
  Normal = (0,0,1)
  Start = (-6300,4600,0)
FEATURE [App::FeaturePython] Dimension034  # Draft dimension (typed FeaturePython)
  Diameter = false
  Dimline = (-6051.21,1110.73,0)
  Direction = (0,0,0)
  Distance = 970.672
  End = (-6400,1000,0)
  Normal = (0,0,1)
  Start = (-6615.34,1946.48,0)
FEATURE [App::FeaturePython] Dimension035  # Draft dimension (typed FeaturePython)
  Diameter = false
  Dimline = (-4862.88,4244.8,0)
  Direction = (0,0,0)
  Distance = 1765.53
  End = (-4862.88,4438.07,0)
  Normal = (0,0,1)
  Start = (-6628.4,4438.07,0)
FEATURE [App::FeaturePython] Dimension036  # Draft dimension (typed FeaturePython)
  Diameter = false
  Dimline = (-1500,4400,0)
  Direction = (0,0,0)
  Distance = 1300
  End = (-1500,4600,0)
  Normal = (0,0,1)
  Start = (-2800,4600,0)
FEATURE [App::FeaturePython] Dimension037  # Draft dimension (typed FeaturePython)
  Diameter = false
  Dimline = (-1600,1000,0)
  Direction = (0,0,0)
  Distance = 224.608
  End = (-1451.97,1019.32,0)
  Normal = (0,0,1)
  Start = (-1451.97,1243.93,0)
FEATURE [App::FeaturePython] Dimension039  # Draft dimension (typed FeaturePython)
  Diameter = false
  Dimline = (2600,-200,0)
  Direction = (0,0,0)
  Distance = 1500
  End = (2600,-500,0)
  Normal = (0,0,1)
  Start = (1100,-500,0)
FEATURE [App::FeaturePython] Dimension040  # Draft dimension (typed FeaturePython)
  Diameter = false
  Dimline = (2400,-500,0)
  Direction = (0,0,0)
  Distance = 2200
  End = (2100,-500,0)
  Normal = (0,0,1)
  Start = (2100,-2700,0)
FEATURE [App::FeaturePython] Dimension041  # Draft dimension (typed FeaturePython)
  Diameter = false
  Dimline = (8200,-1100,0)
  Direction = (0,0,0)
  Distance = 3700
  End = (8400,-700,0)
  Normal = (0,0,1)
  Start = (4700,-700,0)
FEATURE [App::FeaturePython] Dimension042  # Draft dimension (typed FeaturePython)
  Diameter = false
  Dimline = (7500,-1800,0)
  Direction = (0,0,0)
  Distance = 3600
  End = (8000,-2700,0)
  Normal = (0,0,1)
  Start = (8000,900,0)
FEATURE [Image::ImagePlane] flat32
  XSize = 18186.9
  YSize = 13380.6
FEATURE [App::FeaturePython] Dimension043  # Draft dimension (typed FeaturePython)
  Diameter = false
  Dimline = (1200,200,0)
  Direction = (0,0,0)
  Distance = 3595.57
  End = (2091.04,900,0)
  Normal = (0,0,1)
  Start = (2091.04,-2695.57,0)
FEATURE [App::FeaturePython] Dimension048  # Draft dimension (typed FeaturePython)
  Diameter = false
  Dimline = (2500,-400,0)
  Direction = (0,0,0)
  Distance = 5967.06
  End = (2400,130.071,0)
  Normal = (0,0,1)
  Start = (8367.06,130.071,0)
FEATURE [App::FeaturePython] Dimension050  # Draft dimension (typed FeaturePython)
  Diameter = false
  Dimline = (4800,1100,0)
  Direction = (0,0,0)
  Distance = 2300
  End = (4700,700,0)
  Normal = (0,0,1)
  Start = (2400,700,0)
FEATURE [App::FeaturePython] Dimension051  # Draft dimension (typed FeaturePython)
  Diameter = false
  Dimline = (2500,2000,0)
  Direction = (0,0,0)
  Distance = 4440.94
  End = (2360,1491.74,0)
  Normal = (0,0,1)
  Start = (6800.94,1491.74,0)
FEATURE [App::FeaturePython] Dimension052  # Draft dimension (typed FeaturePython)
  Diameter = false
  Dimline = (2400,2200,0)
  Direction = (0,0,0)
  Distance = 3877.58
  End = (2400,1998.9,0)
  Normal = (0,0,1)
  Start = (-1477.58,1998.9,0)
FEATURE [App::FeaturePython] Dimension053  # Draft dimension (typed FeaturePython)
  Diameter = false
  Dimline = (-1628.81,3962.71,0)
  Direction = (0,0,0)
  Distance = 5159.55
  End = (-1477.58,4304.72,0)
  Normal = (0,0,1)
  Start = (-6637.14,4304.72,0)
FEATURE [App::FeaturePython] Dimension054  # Draft dimension (typed FeaturePython)
  Diameter = false
  Dimline = (6800.94,3439.56,0)
  Direction = (0,0,0)
  Distance = 4202.48
  End = (6800.94,4077.61,0)
  Normal = (0,0,1)
  Start = (2598.46,4077.61,0)
FEATURE [App::FeaturePython] Dimension055  # Draft dimension (typed FeaturePython)
  Diameter = false
  Dimline = (4710.2,-1714.6,0)
  Direction = (0,0,0)
  Distance = 3656.86
  End = (4710.2,-2213.58,0)
  Normal = (0,0,1)
  Start = (8367.06,-2213.58,0)
FEATURE [Part::Part2DObjectPython] Rectangle023  # Draft 2D object (typed FeaturePython)
  Area = 653363
  ChamferSize = 0
  Columns = 1
  FilletRadius = 0
  Height = 422.279
  Length = 1547.23
  MakeFace = true
  Placement = pos=(5200,400,0) rot=(0,0,1;0rad)
  Rows = 1
FEATURE [App::Point] Origin001  label="Origin"
  Role = Origin
FEATURE [Part::Part2DObjectPython] Rectangle027  # Draft 2D object (typed FeaturePython)
  Area = 1200000
  ChamferSize = 0
  Columns = 1
  FilletRadius = 0
  Height = 400
  Length = 3000
  MakeFace = true
  Placement = pos=(2800,1000,0) rot=(0,0,1;0rad)
  Rows = 1
FEATURE [Part::Part2DObjectPython] Rectangle028  # Draft 2D object (typed FeaturePython)
  Area = 2.8e+06
  ChamferSize = 0
  Columns = 1
  FilletRadius = 0
  Height = 1400
  Length = 2000
  MakeFace = true
  Placement = pos=(4200,1900,0) rot=(0,0,1;0rad)
  Rows = 1
FEATURE [Part::Part2DObjectPython] Rectangle029  # Draft 2D object (typed FeaturePython)
  Area = 400000
  ChamferSize = 0
  Columns = 1
  FilletRadius = 0
  Height = 800
  Length = 500
  MakeFace = true
  Placement = pos=(3300,3700,0) rot=(0,0,1;0rad)
  Rows = 1
FEATURE [Part::Part2DObjectPython] Rectangle030  # Draft 2D object (typed FeaturePython)
  Area = 951766
  ChamferSize = 0
  Columns = 1
  FilletRadius = 0
  Height = 528.759
  Length = 1800
  MakeFace = true
  Placement = pos=(3897.25,4100,0) rot=(0,0,1;0rad)
  Rows = 1
FEATURE [Part::Part2DObjectPython] Rectangle031  # Draft 2D object (typed FeaturePython)
  Area = 400000
  ChamferSize = 0
  Columns = 1
  FilletRadius = 0
  Height = 1000
  Length = 400
  MakeFace = true
  Placement = pos=(2600,2400,0) rot=(0,0,1;0rad)
  Rows = 1
